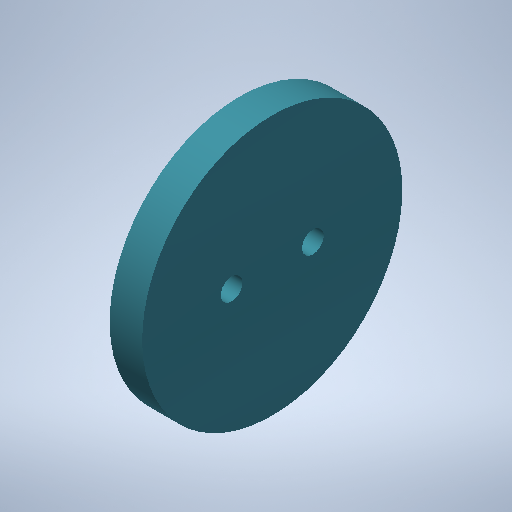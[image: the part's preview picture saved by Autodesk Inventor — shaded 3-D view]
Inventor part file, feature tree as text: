
AUTODESK INVENTOR PART (.ipt)
format: ipt  version: 2025.1 (Build 291241000, 241)  size: 278,528 bytes
history: native  units: in
note: dims shown in document units (in); Inventor stores cm internally (conversion verified against a paired STEP export)
features: extrude x1, sketch x1
ambient origin geometry x8: Origin, YZ Plane, XZ Plane, XY Plane, X Axis, Y Axis, Z Axis, Center Point
bodies: Solid2 (feature_tree)
feature tree (2):
  extrude  "Extrusion16"  Depth=0.1181in
  sketch  "Sketch19"  dims[d111=0.9449in d112=0.0787in d113=0.1476in d114=0.1181in d115=0.0in d116=0.0in d117=0.0in d118=0.0in d119=0.0in]
